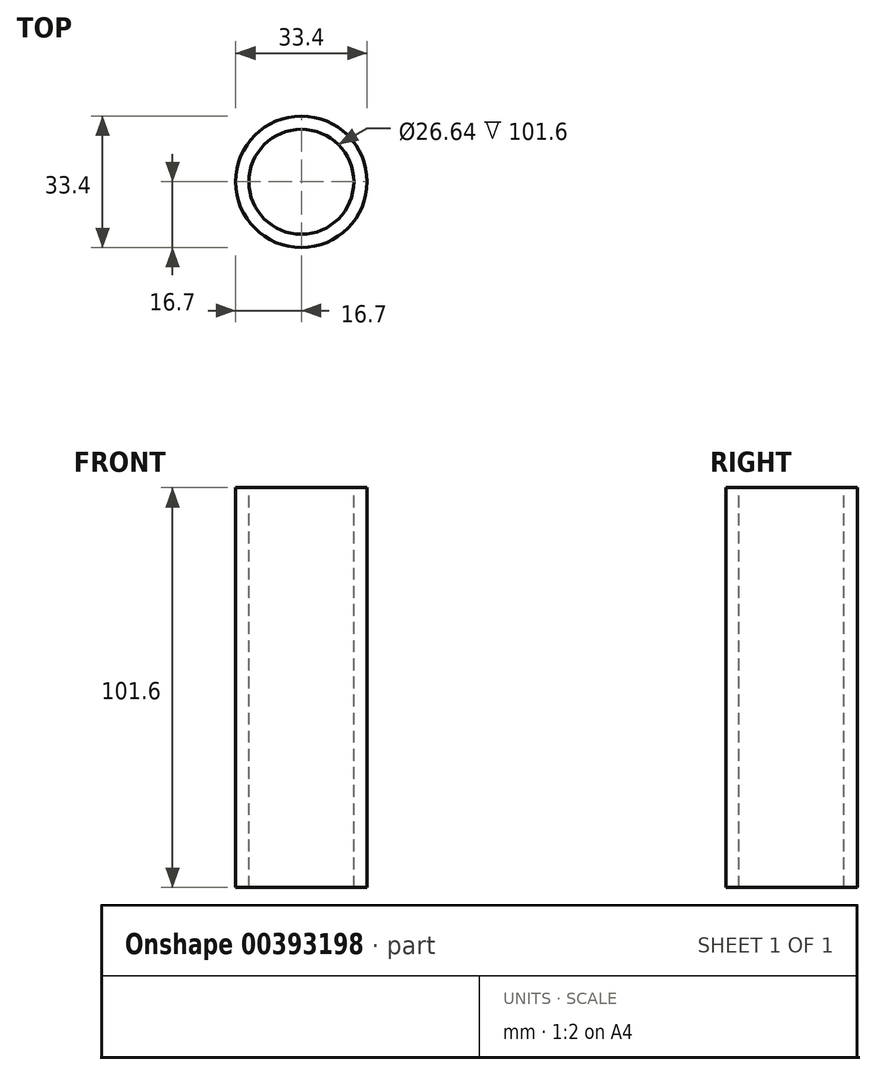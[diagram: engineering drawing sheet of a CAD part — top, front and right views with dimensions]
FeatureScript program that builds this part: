
annotation { "Feature Type Name" : "Feature", "Feature Type Description" : "" }
export const myFeature = defineFeature(function(context is Context, id is Id, definition is map)
    precondition{}
    {
        {
            var Q0;
            Q0=qCreatedBy(makeId("Top.planeOp"),FACE);
            var sketch = newSketch(context, id + "F0", { "sketchPlane" : qUnion([Q0])});
            skCircle(sketch, "E0", {"center": v(0, 0) * mm, "radius": 16.7 * mm});
            skSolve(sketch);
        }
        {
            var Q0;
            Q0 = qSketchRegion(id + "F0", true);
            extrude(context, id + "F1", {"entities" : qUnion([Q0]), "endBound" : BoundingType.SYMMETRIC, "depth" : 101.6 * mm});
        }
        {
            var Q0;
            Q0=makeQuery(id+"F1.opExtrude","CAP_FACE",FACE,{"disambiguationData":[OSD([sQuery(id+"F0.wireOp",EDGE,"E0")])],"isStart":false});
            var sketch = newSketch(context, id + "F2", { "sketchPlane" : qUnion([Q0])});
            skCircle(sketch, "E1", {"center": v(0, 0) * mm, "radius": 13.32 * mm});
            skSolve(sketch);
        }
        {
            var Q0;
            Q0=sQuery(id+"F2.wireOp",VERTEX,"E1.center");
            var Q1;
            Q1=makeQuery(id+"F1.opExtrude","SWEPT_BODY",BODY,{"disambiguationData":[OSD([sQuery(id+"F0.wireOp",EDGE,"E0")])]});
            hole(context, id + "F3", {"style" : HoleStyle.SIMPLE, "endStyle" : HoleEndStyle.THROUGH, "holeDiameter" : 26.64 * mm, "isTappedThrough" : true, "tappedDepth" : 12.7 * mm, "tapClearance" : 3, "locations" : qUnion([Q0]), "scope" : qUnion([Q1])});
        }
    });
